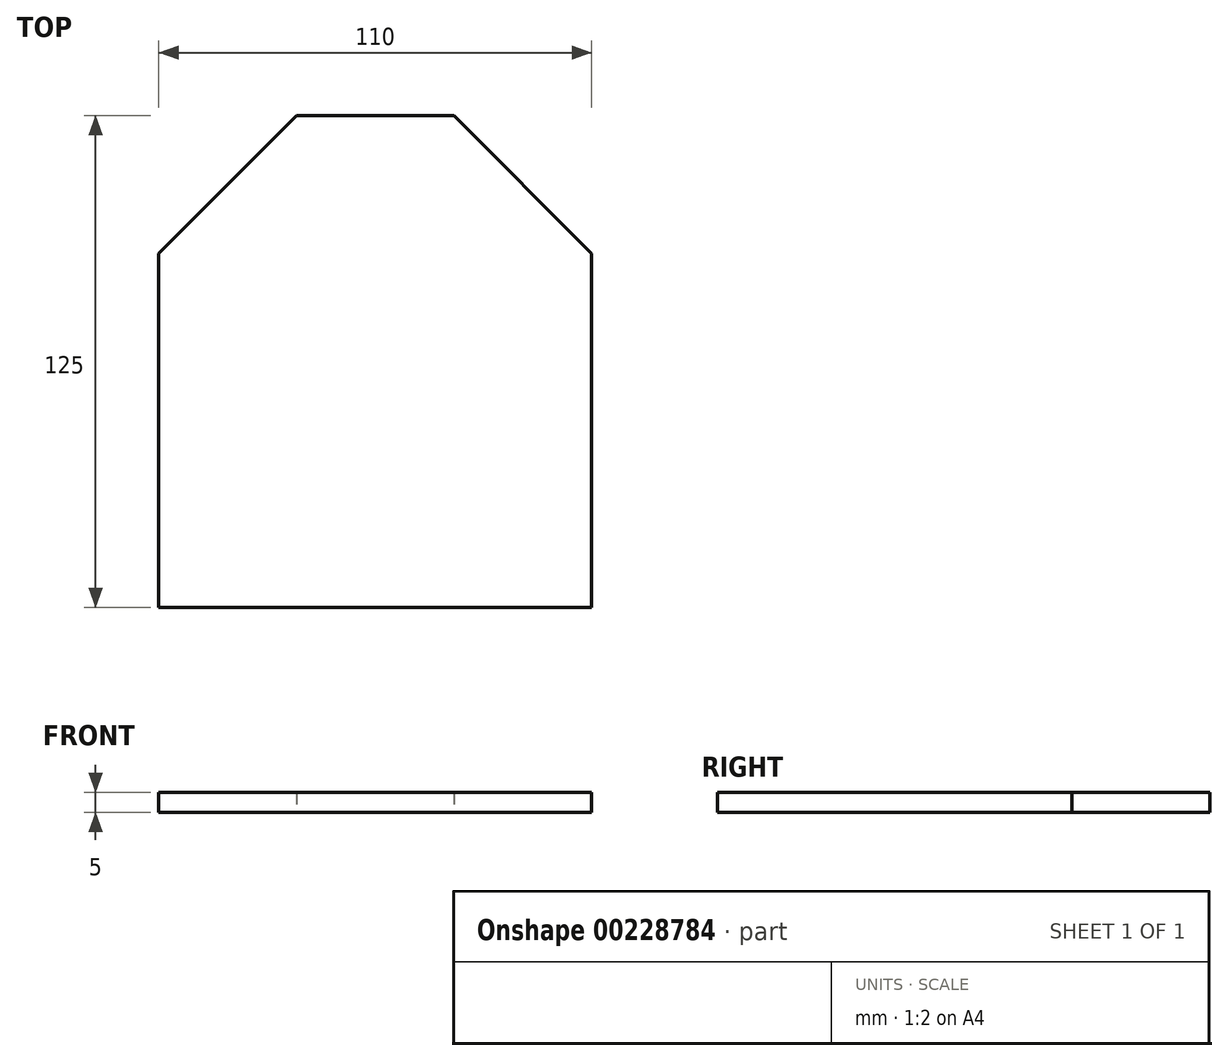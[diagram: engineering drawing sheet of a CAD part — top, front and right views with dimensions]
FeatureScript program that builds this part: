
annotation { "Feature Type Name" : "Feature", "Feature Type Description" : "" }
export const myFeature = defineFeature(function(context is Context, id is Id, definition is map)
    precondition{}
    {
        {
            var Q0;
            Q0=qCreatedBy(makeId("Top.planeOp"),FACE);
            var sketch = newSketch(context, id + "F0", { "sketchPlane" : qUnion([Q0])});
            skLineSegment(sketch, "E0", {"start": v(0, -62.5) * mm, "end": v(0, 62.5) * mm, "construction": true});
            skLineSegment(sketch, "E1", {"start": v(-55, 0) * mm, "end": v(55, 0) * mm, "construction": true});
            skLineSegment(sketch, "E2.bottom", {"start": v(-20, 62.5) * mm, "end": v(55, 62.5) * mm});
            skLineSegment(sketch, "E2.top", {"start": v(-55, -62.5) * mm, "end": v(55, -62.5) * mm});
            skLineSegment(sketch, "E2.left", {"start": v(-55, 27.5) * mm, "end": v(-55, -62.5) * mm});
            skLineSegment(sketch, "E2.right", {"start": v(55, 62.5) * mm, "end": v(55, -62.5) * mm});
            skLineSegment(sketch, "E3", {"start": v(-55, 27.5) * mm, "end": v(-20, 62.5) * mm});
            skLineSegment(sketch, "E4.MirrorCS", {"start": v(55, 27.5) * mm, "end": v(20, 62.5) * mm});
            skPoint(sketch, "E5.orphan", {"position": v(-55, 62.5) * mm});
            skSolve(sketch);
        }
        {
            var Q0;
            {var subQ1=sQuery(id+"F0.wireOp",EDGE,"E2.top");Q0=makeQuery(id+"F0.imprint","IMPRINT",FACE,{"disambiguationData":[TD([[makeQuery(id+"F0.imprint","IMPRINT",EDGE,{"derivedFrom":subQ1}),1.0]])]});}
            extrude(context, id + "F1", {"entities" : qUnion([Q0]), "depth" : 5 * mm});
        }
    });
